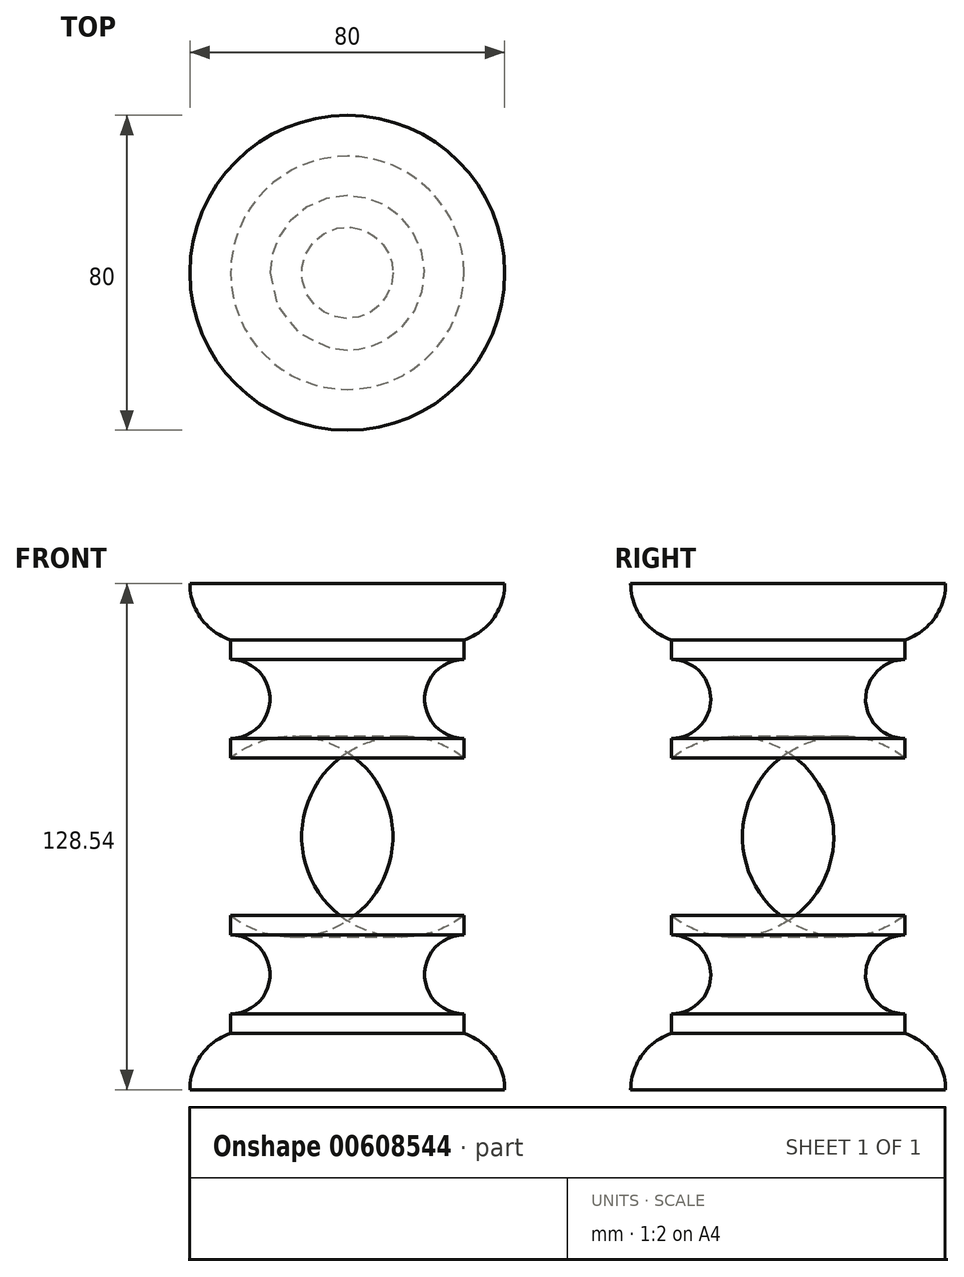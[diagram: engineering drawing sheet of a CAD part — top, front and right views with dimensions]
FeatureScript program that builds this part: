
annotation { "Feature Type Name" : "Feature", "Feature Type Description" : "" }
export const myFeature = defineFeature(function(context is Context, id is Id, definition is map)
    precondition{}
    {
        {
            var Q0;
            Q0=qCreatedBy(makeId("Front.planeOp"),FACE);
            var sketch = newSketch(context, id + "F0", { "sketchPlane" : qUnion([Q0])});
            skLineSegment(sketch, "E0", {"start": v(0, 0) * mm, "end": v(0, 250) * mm, "construction": true});
            skLineSegment(sketch, "E1", {"start": v(0, 250) * mm, "end": v(40, 250) * mm});
            skArc(sketch, "E2", {"start": v(29.62, 235.73) * mm, "mid": v(37.13, 241.18) * mm, "end": v(40, 250) * mm});
            skLineSegment(sketch, "E3", {"start": v(29.62, 235.73) * mm, "end": v(29.62, 230.73) * mm});
            skArc(sketch, "E4", {"start": v(29.62, 230.73) * mm, "mid": v(19.62, 220.73) * mm, "end": v(29.62, 210.73) * mm});
            skLineSegment(sketch, "E5", {"start": v(29.62, 210.73) * mm, "end": v(29.62, 205.73) * mm});
            skArc(sketch, "E6", {"start": v(29.62, 165.73) * mm, "mid": v(39.32, 185.73) * mm, "end": v(29.62, 205.73) * mm});
            skLineSegment(sketch, "E7", {"start": v(13.86, 185.73) * mm, "end": v(83.35, 185.73) * mm, "construction": true});
            skArc(sketch, "E8.MirrorCS", {"start": v(29.62, 135.73) * mm, "mid": v(37.13, 130.28) * mm, "end": v(40, 121.46) * mm});
            skLineSegment(sketch, "E9.MirrorCS", {"start": v(29.62, 135.73) * mm, "end": v(29.62, 140.73) * mm});
            skArc(sketch, "E10.MirrorCS", {"start": v(29.62, 140.73) * mm, "mid": v(19.62, 150.73) * mm, "end": v(29.62, 160.73) * mm});
            skLineSegment(sketch, "E11.MirrorCS", {"start": v(29.62, 160.73) * mm, "end": v(29.62, 165.73) * mm});
            skLineSegment(sketch, "E12.MirrorCS", {"start": v(0, 121.46) * mm, "end": v(40, 121.46) * mm});
            skLineSegment(sketch, "E13", {"start": v(0, 250) * mm, "end": v(0, 121.46) * mm});
            skLineSegment(sketch, "E14", {"start": v(0, 0) * mm, "end": v(70, 0) * mm});
            skArc(sketch, "E15", {"start": v(82.79, 19.6) * mm, "mid": v(75.04, 10.69) * mm, "end": v(70, 0) * mm});
            skLineSegment(sketch, "E16", {"start": v(82.79, 19.6) * mm, "end": v(57.28, 19.6) * mm});
            skSolve(sketch);
        }
        {
            var Q0;
            Q0=makeQuery(id+"F0.imprint","IMPRINT",FACE,{"disambiguationData":[TD([[makeQuery(id+"F0.imprint","IMPRINT",EDGE,{"derivedFrom":sQuery(id+"F0.wireOp",EDGE,"E1")}),-1.0]])]});
            var Q1;
            Q1=sQuery(id+"F0.wireOp",EDGE,"E0");
            revolve(context, id + "F1", {"entities" : qUnion([Q0]), "axis" : qUnion([Q1]), "revolveType" : RevolveType.FULL});
        }
    });
